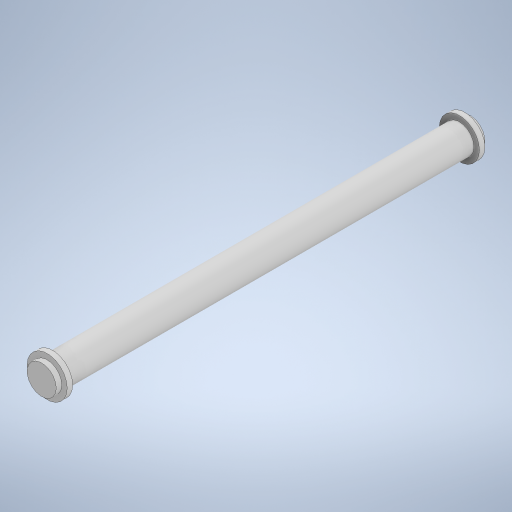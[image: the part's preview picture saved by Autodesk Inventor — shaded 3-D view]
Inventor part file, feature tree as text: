
AUTODESK INVENTOR PART (.ipt)
format: ipt  version: 2023 (Build 270158000, 158)  size: 255,488 bytes
history: native  units: in
note: dims shown in document units (in); Inventor stores cm internally (conversion verified against a paired STEP export)
features: extrude x5, sketch x5
ambient origin geometry x8: Origin, YZ Plane, XZ Plane, XY Plane, X Axis, Y Axis, Z Axis, Center Point
bodies: Solid1 (feature_tree)
feature tree (10):
  extrude  "Extrusion1"  Depth=111.5in TaperAngle=0.0deg
  extrude  "Extrusion2"  Depth=1.5in TaperAngle=0.0deg
  extrude  "Extrusion3"  Depth=1.5in TaperAngle=0.0deg
  extrude  "Extrusion4"  [1 undecoded]
  extrude  "Extrusion5"  [1 undecoded]
  sketch  "Sketch1"  dims[d0=8.0in d1=111.5in d2=0.0in]
  sketch  "Sketch2"  dims[d3=11.0in d4=1.5in d5=0.0in]
  sketch  "Sketch3"  dims[d6=1.5in d7=0.0in d8=1.5in d9=0.0in]
  sketch  "Sketch4"  dims[d10=1.5in d11=0.0in]
  sketch  "Sketch5"
note: 2 required parameter values undecoded (feature->parameter linkage not recoverable at this tier; creation-order binding heuristic only, values carry confidence <= 0.55)
